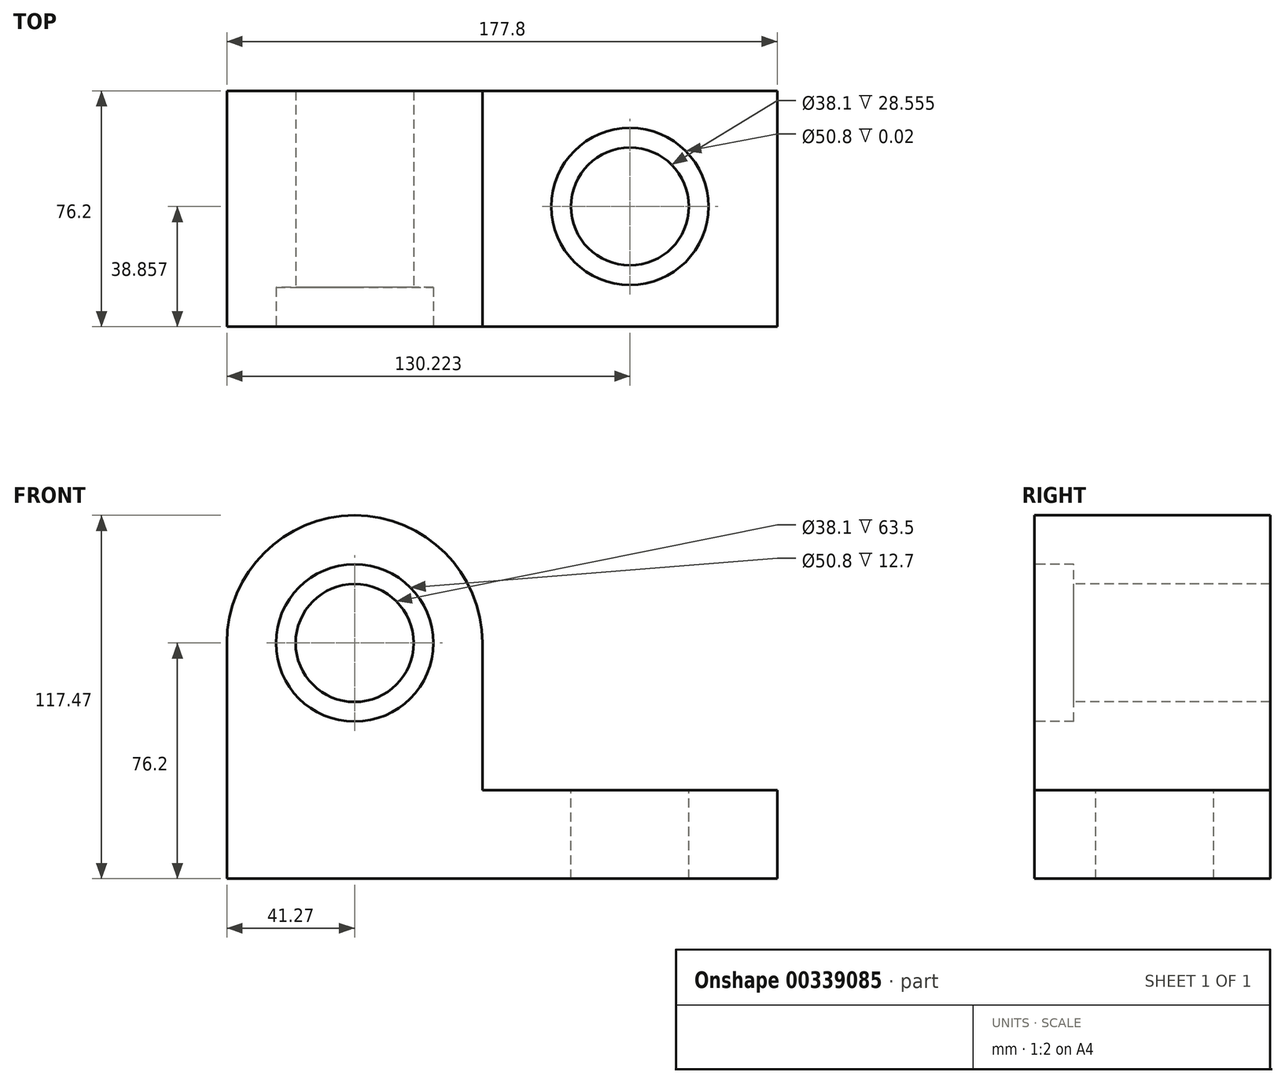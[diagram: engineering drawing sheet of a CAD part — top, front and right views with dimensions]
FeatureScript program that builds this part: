
annotation { "Feature Type Name" : "Feature", "Feature Type Description" : "" }
export const myFeature = defineFeature(function(context is Context, id is Id, definition is map)
    precondition{}
    {
        {
            var Q0;
            Q0=qCreatedBy(makeId("Front.planeOp"),FACE);
            var sketch = newSketch(context, id + "F0", { "sketchPlane" : qUnion([Q0])});
            skCircle(sketch, "E0", {"center": v(0, 0) * mm, "radius": 19.05 * mm});
            skCircle(sketch, "E1", {"center": v(0, 0) * mm, "radius": 41.28 * mm});
            skLineSegment(sketch, "E2", {"start": v(-41.28, 0) * mm, "end": v(-41.27, -76.2) * mm});
            skLineSegment(sketch, "E3", {"start": v(41.27, 0) * mm, "end": v(41.28, -76.2) * mm});
            skLineSegment(sketch, "E4", {"start": v(-41.28, -76.2) * mm, "end": v(136.53, -76.2) * mm});
            skLineSegment(sketch, "E5", {"start": v(136.53, -76.2) * mm, "end": v(136.53, -47.62) * mm});
            skLineSegment(sketch, "E6", {"start": v(136.53, -47.62) * mm, "end": v(41.28, -47.62) * mm});
            skSolve(sketch);
        }
        {
            var Q0;
            Q0=makeQuery(id+"F0.imprint","IMPRINT",FACE,{"disambiguationData":[TD([[makeQuery(id+"F0.imprint","IMPRINT",EDGE,{"derivedFrom":sQuery(id+"F0.wireOp",EDGE,"E0")}),-1.0]])]});
            var Q1;
            {var subQ6=sQuery(id+"F0.wireOp",EDGE,"E2");Q1=makeQuery(id+"F0.imprint","IMPRINT",FACE,{"disambiguationData":[TD([[makeQuery(id+"F0.imprint","IMPRINT",EDGE,{"derivedFrom":subQ6}),1.0]])]});}
            var Q2;
            {var subQ4=sQuery(id+"F0.wireOp",EDGE,"E5");Q2=makeQuery(id+"F0.imprint","IMPRINT",FACE,{"disambiguationData":[TD([[makeQuery(id+"F0.imprint","IMPRINT",EDGE,{"derivedFrom":subQ4}),1.0]])]});}
            var Q3;
            Q3=makeQuery(id+"F0.imprint","IMPRINT",FACE,{"disambiguationData":[TD([[makeQuery(id+"F0.imprint","IMPRINT",EDGE,{"derivedFrom":sQuery(id+"F0.wireOp",EDGE,"E0")}),1.0]])]});
            extrude(context, id + "F1", {"entities" : qUnion([Q0, Q1, Q2, Q3]), "oppositeDirection" : true, "depth" : 76.2 * mm});
        }
        {
            var Q0;
            Q0=makeQuery(id+"F1.opExtrude","SWEPT_FACE",FACE,{"disambiguationData":[OSD([sQuery(id+"F0.wireOp",EDGE,"E6")])]});
            var sketch = newSketch(context, id + "F2", { "sketchPlane" : qUnion([Q0])});
            skCircle(sketch, "E7", {"center": v(88.95, 38.86) * mm, "radius": 19.05 * mm});
            skSolve(sketch);
        }
        {
            var Q0;
            Q0=sQuery(id+"F2.wireOp",VERTEX,"E7.center");
            var Q1;
            Q1=makeQuery(id+"F1.opExtrude","SWEPT_BODY",BODY,{"disambiguationData":[OSD([sQuery(id+"F0.wireOp",EDGE,"E1"),sQuery(id+"F0.wireOp",EDGE,"E2"),sQuery(id+"F0.wireOp",EDGE,"E3"),sQuery(id+"F0.wireOp",EDGE,"E4"),sQuery(id+"F0.wireOp",EDGE,"E5"),sQuery(id+"F0.wireOp",EDGE,"E6")])]});
            hole(context, id + "F3", {"style" : HoleStyle.C_BORE, "endStyle" : HoleEndStyle.THROUGH, "holeDiameter" : 38.1 * mm, "cBoreDiameter" : 50.8 * mm, "cBoreDepth" : 1 / 50.8 * mm, "isTappedThrough" : true, "tappedDepth" : 12.7 * mm, "tapClearance" : 3, "locations" : qUnion([Q0]), "scope" : qUnion([Q1])});
        }
        {
            var Q0;
            Q0 = qSketchRegion(id + "F0", true);
            var sketch = newSketch(context, id + "F4", { "sketchPlane" : qUnion([Q0])});
            skCircle(sketch, "E8", {"center": v(0, 0) * mm, "radius": 7.1 * mm});
            skSolve(sketch);
        }
        {
            var Q0;
            Q0=sQuery(id+"F4.wireOp",VERTEX,"E8.center");
            var Q1;
            Q1=makeQuery(id+"F1.opExtrude","SWEPT_BODY",BODY,{"disambiguationData":[OSD([sQuery(id+"F0.wireOp",EDGE,"E1"),sQuery(id+"F0.wireOp",EDGE,"E2"),sQuery(id+"F0.wireOp",EDGE,"E3"),sQuery(id+"F0.wireOp",EDGE,"E4"),sQuery(id+"F0.wireOp",EDGE,"E5"),sQuery(id+"F0.wireOp",EDGE,"E6")])]});
            hole(context, id + "F5", {"style" : HoleStyle.C_BORE, "endStyle" : HoleEndStyle.THROUGH, "holeDiameter" : 38.1 * mm, "cBoreDiameter" : 50.8 * mm, "cBoreDepth" : 12.7 * mm, "isTappedThrough" : true, "tappedDepth" : 12.7 * mm, "tapClearance" : 3, "locations" : qUnion([Q0]), "scope" : qUnion([Q1])});
        }
    });
